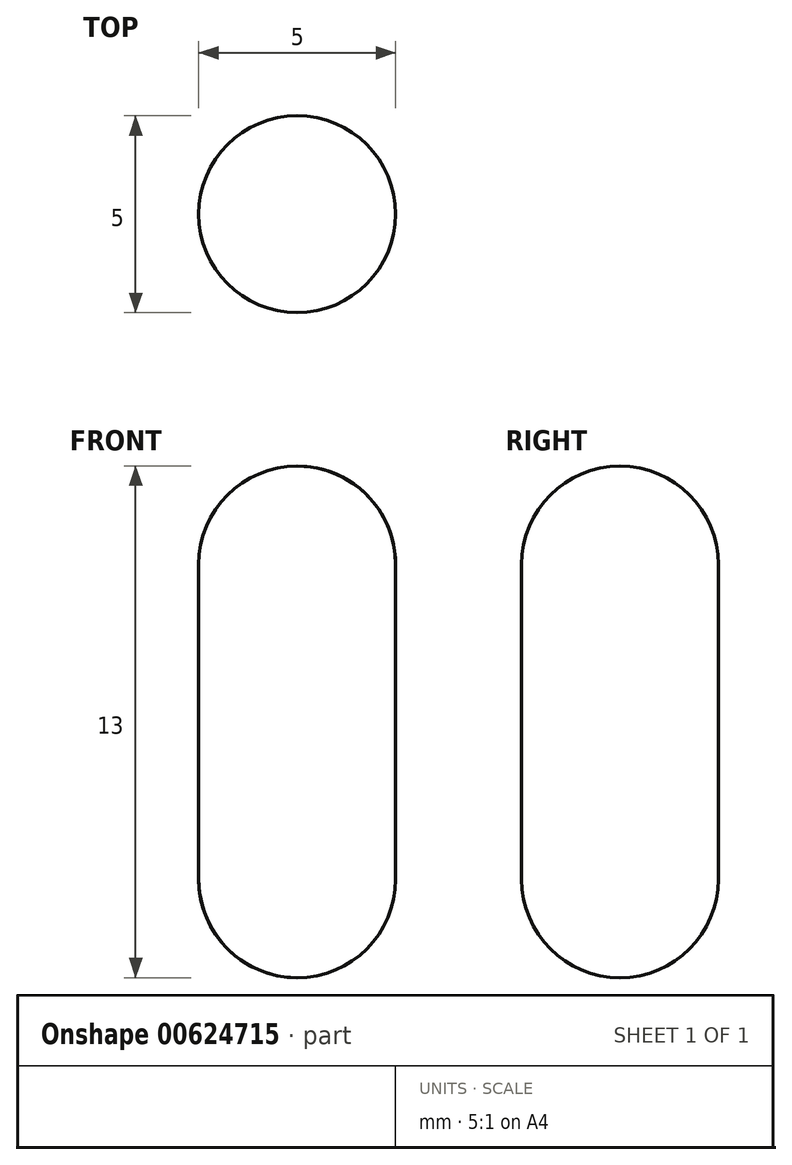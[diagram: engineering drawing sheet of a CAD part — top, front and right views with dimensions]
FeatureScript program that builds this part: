
annotation { "Feature Type Name" : "Feature", "Feature Type Description" : "" }
export const myFeature = defineFeature(function(context is Context, id is Id, definition is map)
    precondition{}
    {
        {
            var Q0;
            Q0=qCreatedBy(makeId("Front.planeOp"),FACE);
            var sketch = newSketch(context, id + "F0", { "sketchPlane" : qUnion([Q0])});
            skArc(sketch, "E0", {"start": v(0, 10.5) * mm, "mid": v(-1.77, 9.77) * mm, "end": v(-2.5, 8) * mm});
            skArc(sketch, "E1", {"start": v(-2.5, 0) * mm, "mid": v(-1.77, -1.77) * mm, "end": v(0, -2.5) * mm});
            skLineSegment(sketch, "E2", {"start": v(-2.5, 8) * mm, "end": v(-2.5, 0) * mm});
            skLineSegment(sketch, "E3", {"start": v(0, 10.5) * mm, "end": v(0, -2.5) * mm});
            skSolve(sketch);
        }
        {
            var Q0;
            Q0=makeQuery(id+"F0.imprint","IMPRINT",FACE,{"disambiguationData":[TD([[makeQuery(id+"F0.imprint","IMPRINT",EDGE,{"derivedFrom":sQuery(id+"F0.wireOp",EDGE,"E0")}),1.0]])]});
            var Q1;
            Q1=sQuery(id+"F0.wireOp",EDGE,"E3");
            revolve(context, id + "F1", {"entities" : qUnion([Q0]), "axis" : qUnion([Q1]), "revolveType" : RevolveType.FULL});
        }
    });
